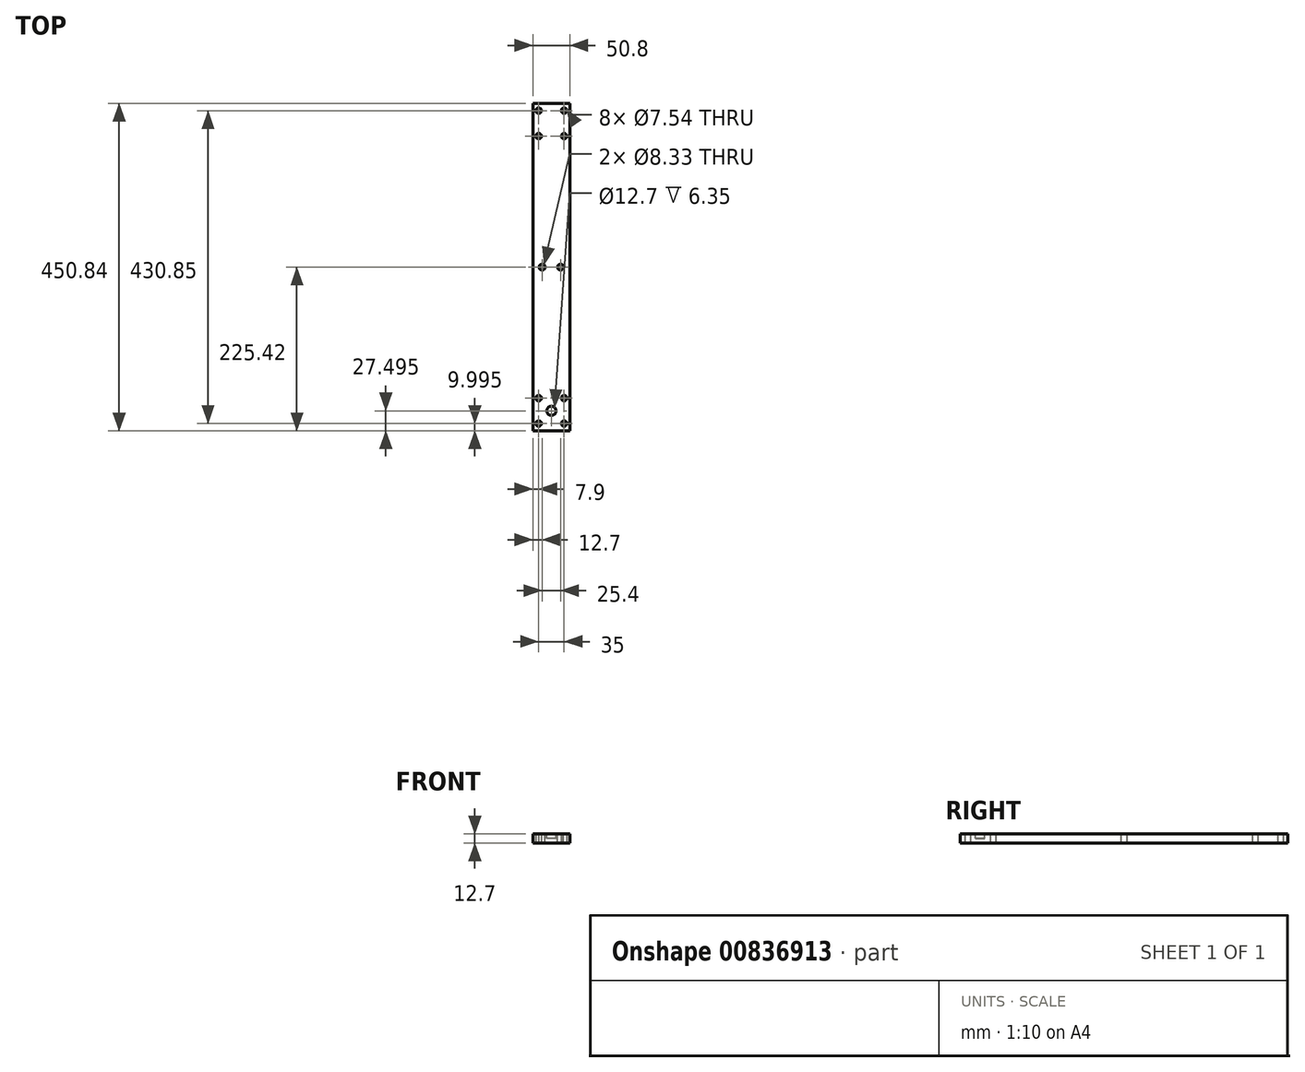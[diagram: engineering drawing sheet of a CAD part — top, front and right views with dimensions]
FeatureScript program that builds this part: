
annotation { "Feature Type Name" : "Feature", "Feature Type Description" : "" }
export const myFeature = defineFeature(function(context is Context, id is Id, definition is map)
    precondition{}
    {
        {
            var Q0;
            Q0=qCreatedBy(makeId("Top.planeOp"),FACE);
            var sketch = newSketch(context, id + "F0", { "sketchPlane" : qUnion([Q0])});
            skLineSegment(sketch, "E0.bottom", {"start": v(25.4, -225.43) * mm, "end": v(-25.4, -225.43) * mm});
            skLineSegment(sketch, "E0.top", {"start": v(25.4, 225.43) * mm, "end": v(-25.4, 225.43) * mm});
            skLineSegment(sketch, "E0.left", {"start": v(25.4, -225.43) * mm, "end": v(25.4, 225.43) * mm});
            skLineSegment(sketch, "E0.right", {"start": v(-25.4, -225.43) * mm, "end": v(-25.4, 225.43) * mm});
            skPoint(sketch, "E0.middle", {"position": v(0, 0) * mm});
            skLineSegment(sketch, "E1.bottom", {"start": v(17.5, -215.43) * mm, "end": v(-17.5, -215.43) * mm, "construction": true});
            skLineSegment(sketch, "E1.top", {"start": v(17.5, -180.43) * mm, "end": v(-17.5, -180.43) * mm, "construction": true});
            skLineSegment(sketch, "E1.left", {"start": v(17.5, -215.43) * mm, "end": v(17.5, -180.43) * mm, "construction": true});
            skLineSegment(sketch, "E1.right", {"start": v(-17.5, -215.43) * mm, "end": v(-17.5, -180.43) * mm, "construction": true});
            skPoint(sketch, "E1.middle", {"position": v(0, -197.93) * mm});
            skPoint(sketch, "E1.middle.positionSnap0", {"position": v(0, -225.43) * mm});
            skPoint(sketch, "E1.centerSnap0", {"position": v(0, -225.43) * mm});
            skCircle(sketch, "E2", {"center": v(-17.5, -215.43) * mm, "radius": 3.77 * mm});
            skCircle(sketch, "E3", {"center": v(17.5, -215.43) * mm, "radius": 3.77 * mm});
            skCircle(sketch, "E4", {"center": v(-17.5, -180.43) * mm, "radius": 3.77 * mm});
            skCircle(sketch, "E5", {"center": v(17.5, -180.43) * mm, "radius": 3.77 * mm});
            skCircle(sketch, "E6.MirrorC", {"center": v(-17.5, 215.43) * mm, "radius": 3.77 * mm});
            skCircle(sketch, "E7.MirrorC", {"center": v(17.5, 180.43) * mm, "radius": 3.77 * mm});
            skCircle(sketch, "E8.MirrorC", {"center": v(17.5, 215.43) * mm, "radius": 3.77 * mm});
            skCircle(sketch, "E9.MirrorC", {"center": v(-17.5, 180.43) * mm, "radius": 3.77 * mm});
            skPoint(sketch, "E10.MirrorP", {"position": v(0, 225.43) * mm});
            skLineSegment(sketch, "E11.MirrorCS", {"start": v(-17.5, 215.43) * mm, "end": v(-17.5, 180.43) * mm, "construction": true});
            skLineSegment(sketch, "E12.MirrorCS", {"start": v(17.5, 215.43) * mm, "end": v(17.5, 180.43) * mm, "construction": true});
            skLineSegment(sketch, "E13.MirrorCS", {"start": v(17.5, 180.43) * mm, "end": v(-17.5, 180.43) * mm, "construction": true});
            skPoint(sketch, "E14.MirrorP", {"position": v(0, 197.93) * mm});
            skLineSegment(sketch, "E15.MirrorCS", {"start": v(17.5, 215.43) * mm, "end": v(-17.5, 215.43) * mm, "construction": true});
            skSolve(sketch);
        }
        {
            var Q0;
            Q0 = qSketchRegion(id + "F0", true);
            extrude(context, id + "F1", {"entities" : qUnion([Q0]), "depth" : 12.7 * mm, "offsetDistance" : 25.4 * mm});
        }
        {
            var Q0;
            Q0=makeQuery(id+"F1.opExtrude","CAP_FACE",FACE,{"disambiguationData":[OSD([sQuery(id+"F0.wireOp",EDGE,"E0.bottom"),sQuery(id+"F0.wireOp",EDGE,"E0.top"),sQuery(id+"F0.wireOp",EDGE,"E0.left"),sQuery(id+"F0.wireOp",EDGE,"E0.right"),sQuery(id+"F0.wireOp",EDGE,"E2"),sQuery(id+"F0.wireOp",EDGE,"E3"),sQuery(id+"F0.wireOp",EDGE,"E4"),sQuery(id+"F0.wireOp",EDGE,"E5"),sQuery(id+"F0.wireOp",EDGE,"my3Ie493-8Ras-gGrY-rEs4-fJYLENW8QWYO"),sQuery(id+"F0.wireOp",EDGE,"fC7u6OnJ-EDhf-nKqi-uWiA-HPoTwULejLAn"),sQuery(id+"F0.wireOp",EDGE,"LT9rl4th-wM5L-oEv0-TBul-bosC5fCvp1T2"),sQuery(id+"F0.wireOp",EDGE,"yw4JMZ9y-IZ4b-2hsr-5tjQ-qm93wY1FJo5S")])],"isStart":false});
            var sketch = newSketch(context, id + "F2", { "sketchPlane" : qUnion([Q0])});
            skCircle(sketch, "E16", {"center": v(-12.7, 0) * mm, "radius": 4.17 * mm});
            skCircle(sketch, "E17", {"center": v(12.7, 0) * mm, "radius": 4.17 * mm});
            skLineSegment(sketch, "E18", {"start": v(-25.4, 0) * mm, "end": v(-12.7, 0) * mm, "construction": true});
            skLineSegment(sketch, "E19", {"start": v(-12.7, 0) * mm, "end": v(0, 0) * mm, "construction": true});
            skLineSegment(sketch, "E20", {"start": v(12.7, 0) * mm, "end": v(0, 0) * mm, "construction": true});
            skLineSegment(sketch, "E21", {"start": v(12.7, 0) * mm, "end": v(25.4, 0) * mm, "construction": true});
            skSolve(sketch);
        }
        {
            var Q0;
            Q0 = qSketchRegion(id + "F2", true);
            extrude(context, id + "F3", {"entities" : qUnion([Q0]), "operationType" : NewBodyOperationType.REMOVE, "oppositeDirection" : true, "depth" : 25.4 * mm, "offsetDistance" : 25.4 * mm});
        }
        {
            var Q0;
            Q0=makeQuery(id+"F1.opExtrude","CAP_FACE",FACE,{"disambiguationData":[OSD([sQuery(id+"F0.wireOp",EDGE,"E0.bottom"),sQuery(id+"F0.wireOp",EDGE,"E0.top"),sQuery(id+"F0.wireOp",EDGE,"E0.left"),sQuery(id+"F0.wireOp",EDGE,"E0.right"),sQuery(id+"F0.wireOp",EDGE,"E2"),sQuery(id+"F0.wireOp",EDGE,"E3"),sQuery(id+"F0.wireOp",EDGE,"E4"),sQuery(id+"F0.wireOp",EDGE,"E5"),sQuery(id+"F0.wireOp",EDGE,"E6.MirrorC"),sQuery(id+"F0.wireOp",EDGE,"E7.MirrorC"),sQuery(id+"F0.wireOp",EDGE,"E8.MirrorC"),sQuery(id+"F0.wireOp",EDGE,"E9.MirrorC")])],"isStart":false});
            var sketch = newSketch(context, id + "F4", { "sketchPlane" : qUnion([Q0])});
            skPoint(sketch, "E22.centerSnap0", {"position": v(0, 225.43) * mm});
            skCircle(sketch, "E23", {"center": v(0, -197.93) * mm, "radius": 6.35 * mm});
            skPoint(sketch, "E23.centerSnap0", {"position": v(0, -225.43) * mm});
            skLineSegment(sketch, "E24", {"start": v(17.5, -180.43) * mm, "end": v(-17.5, -215.43) * mm});
            skSolve(sketch);
        }
        {
            var Q0;
            Q0 = qSketchRegion(id + "F4", true);
            extrude(context, id + "F5", {"entities" : qUnion([Q0]), "operationType" : NewBodyOperationType.REMOVE, "oppositeDirection" : true, "depth" : 6.35 * mm, "offsetDistance" : 25.4 * mm});
        }
    });
